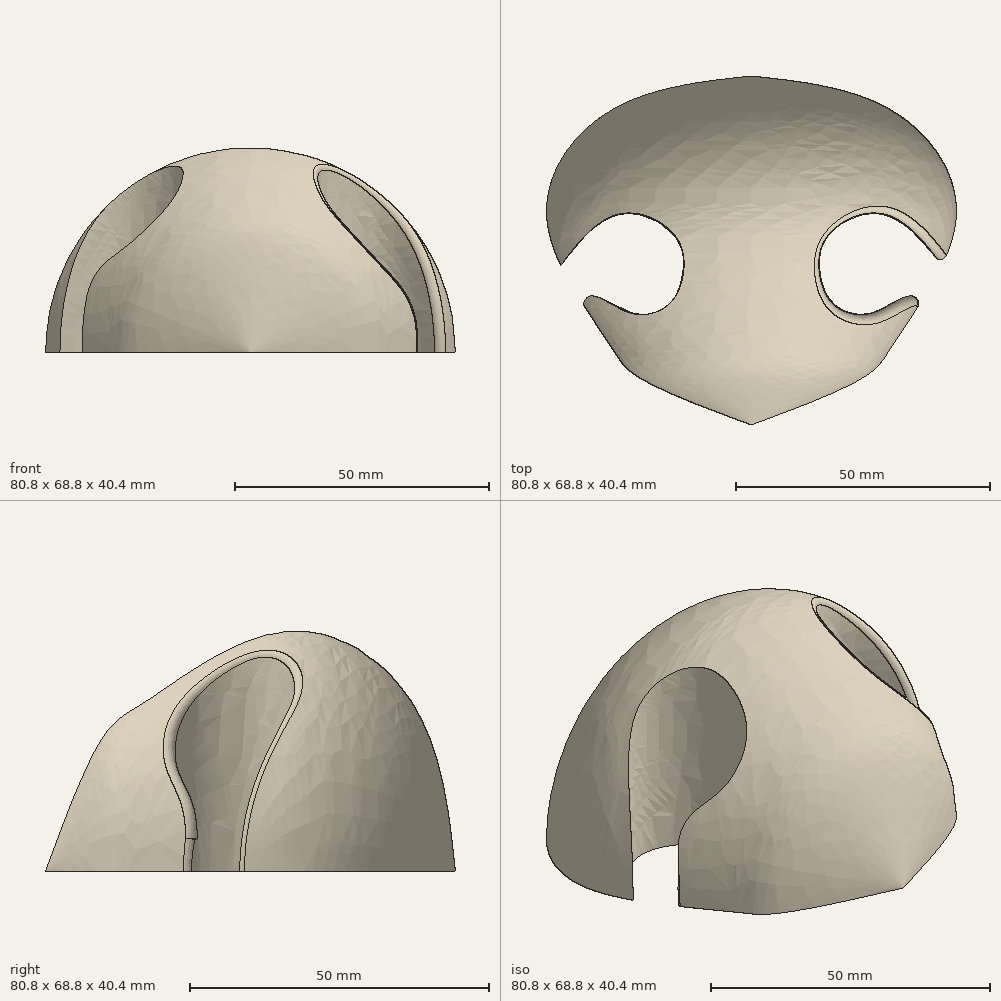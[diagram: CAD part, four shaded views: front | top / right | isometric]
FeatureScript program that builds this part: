
annotation { "Feature Type Name" : "Feature", "Feature Type Description" : "" }
export const myFeature = defineFeature(function(context is Context, id is Id, definition is map)
    precondition{}
    {
        {
            var Q0;
            Q0=qCreatedBy(makeId("Top.planeOp"),FACE);
            var sketch = newSketch(context, id + "F0", { "sketchPlane" : qUnion([Q0])});
            skFitSpline(sketch, "E0", {"points": [v(0, 37.27) * mm, v(28.44, 29.97) * mm, v(40.3, 8.97) * mm, v(28.44, -14.75) * mm, v(23.58, -21.14) * mm, v(0, -31.49) * mm], "startDerivative": vector(132.43, -14.26) * mm, "endDerivative": vector(-134, -49.4) * mm});
            skLineSegment(sketch, "E1", {"start": v(0, 53.4) * mm, "end": v(0, -54.6) * mm});
            skSolve(sketch);
        }
        {
            var Q0;
            {var subQ0=sQuery(id+"F0.wireOp",EDGE,"E0");Q0=makeQuery(id+"F0.imprint","IMPRINT",FACE,{"disambiguationData":[TD([[makeQuery(id+"F0.imprint","IMPRINT",EDGE,{"derivedFrom":subQ0}),-1.0]])]});}
            var Q1;
            Q1 = qSketchRegion(id + "FBp7yYcEycIipKS_1", true);
            var Q2;
            Q2=sQuery(id+"F0.wireOp",EDGE,"E1");
            revolve(context, id + "F1", {"surfaceOperationType" : NewSurfaceOperationType.NEW, "entities" : qUnion([Q0, Q1]), "axis" : qUnion([Q2]), "revolveType" : RevolveType.ONE_DIRECTION, "angle" : 180 * degree});
        }
        {
            var Q0;
            Q0=qCreatedBy(makeId("Top.planeOp"),FACE);
            var sketch = newSketch(context, id + "F2", { "sketchPlane" : qUnion([Q0])});
            skFitSpline(sketch, "E2", {"points": [v(40.95, -5.34) * mm, v(26.7, 9.9) * mm, v(15.7, 6.52) * mm, v(13.27, 0) * mm, v(15.97, -7.53) * mm, v(22.75, -9.68) * mm, v(28.64, -7.05) * mm, v(32.1, -6.22) * mm, v(33.13, -7.67) * mm, v(33.2, -7.8) * mm], "startDerivative": vector(-51.36, 80.16) * mm, "endDerivative": vector(2.76, -4.83) * mm});
            skLineSegment(sketch, "E3", {"start": v(40.95, -5.34) * mm, "end": v(33.19, -7.78) * mm});
            skFitSpline(sketch, "E4.MirrorCS", {"points": [v(-40.95, -5.34) * mm, v(-26.7, 9.9) * mm, v(-15.7, 6.52) * mm, v(-13.27, 0) * mm, v(-15.97, -7.53) * mm, v(-22.75, -9.68) * mm, v(-28.64, -7.05) * mm, v(-32.1, -6.22) * mm, v(-33.13, -7.67) * mm, v(-33.2, -7.8) * mm], "startDerivative": vector(51.36, 80.16) * mm, "endDerivative": vector(-2.76, -4.83) * mm});
            skFitSpline(sketch, "E5.MirrorCS", {"points": [v(-40.95, -5.34) * mm, v(-26.7, 9.9) * mm, v(-15.7, 6.52) * mm, v(-13.27, 0) * mm, v(-15.97, -7.53) * mm, v(-22.75, -9.68) * mm, v(-28.64, -7.05) * mm, v(-32.1, -6.22) * mm, v(-33.13, -7.67) * mm, v(-33.2, -7.8) * mm], "startDerivative": vector(51.36, 80.16) * mm, "endDerivative": vector(-2.76, -4.83) * mm});
            skLineSegment(sketch, "E6.MirrorCS", {"start": v(-40.95, -5.34) * mm, "end": v(-33.19, -7.78) * mm});
            skSolve(sketch);
        }
        {
            var Q0;
            Q0 = qSketchRegion(id + "F2", true);
            extrude(context, id + "F3", {"entities" : qUnion([Q0]), "depth" : 76.2 * mm, "offsetDistance" : 25.4 * mm});
        }
        {
            var Q0;
            Q0=makeQuery(id+"F3.opExtrude","SWEPT_BODY",BODY,{"disambiguationData":[OSD([sQuery(id+"F2.wireOp",EDGE,"E2"),sQuery(id+"F2.wireOp",EDGE,"E3")])]});
            var Q1;
            Q1=makeQuery(id+"F3.opExtrude","SWEPT_BODY",BODY,{"disambiguationData":[OSD([sQuery(id+"F2.wireOp",EDGE,"E5.MirrorCS"),sQuery(id+"F2.wireOp",EDGE,"E6.MirrorCS")])]});
            var Q2;
            Q2=makeQuery(id+"F1.opRevolve","SWEPT_BODY",BODY,{"disambiguationData":[OSD([sQuery(id+"F0.wireOp",EDGE,"E0"),sQuery(id+"F0.wireOp",EDGE,"E1")])]});
            booleanBodies(context, id + "F4", {"operationType" : BooleanOperationType.SUBTRACTION, "tools" : qUnion([Q0, Q1]), "targets" : qUnion([Q2])});
        }
        {
            var Q0;
            Q0=makeQuery(id+"F4.opBoolean","INTERSECT",EDGE,{"derivedFrom":[makeQuery(id+"F1.opRevolve","SWEPT_FACE",FACE,{"disambiguationData":[OSD([sQuery(id+"F0.wireOp",EDGE,"E0")])]}),makeQuery(id+"F3.opExtrude","SWEPT_FACE",FACE,{"disambiguationData":[OSD([sQuery(id+"F2.wireOp",EDGE,"E5.MirrorCS")])]})]});
            var Q1;
            Q1=makeQuery(id+"F4.opBoolean","INTERSECT",EDGE,{"derivedFrom":[makeQuery(id+"F1.opRevolve","SWEPT_FACE",FACE,{"disambiguationData":[OSD([sQuery(id+"F0.wireOp",EDGE,"E0")])]}),makeQuery(id+"F3.opExtrude","SWEPT_FACE",FACE,{"disambiguationData":[OSD([sQuery(id+"F2.wireOp",EDGE,"E2")])]})]});
            fillet(context, id + "F5", {"entities" : qUnion([Q0, Q1]), "radius" : 1.27 * mm, "tangentPropagation" : true, "allowEdgeOverflow" : false});
        }
    });
